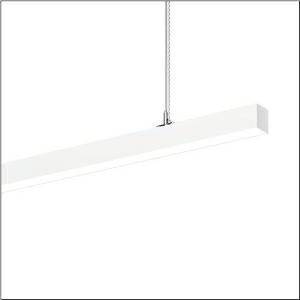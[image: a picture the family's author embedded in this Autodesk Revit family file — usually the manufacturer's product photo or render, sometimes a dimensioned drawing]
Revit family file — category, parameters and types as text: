
# Revit family: silica_r__21_51mx30dc39wb_5262
name_source: partatom
category: Lighting Fixtures
units: mm (PartAtom-declared; Revit-internal decimal feet)

## family parameters
Cut with Voids When Loaded = No
Host = Face
Light Source = No
Part Type = Normal
Room Calculation Point = No
Round Connector Dimension = Use Diameter
Shared = No

## types (1)
- --- (1 x LED, 10520 lm, 68.3 W, 3000K)
    Apparent Load = 68 VA
    CIE Flux Codes = 47 79 96 57 100
    Color Rendering = 80
    Color Temperature = 3000K
    Default Elevation = 1800 mm
    Description = Silica® 21, office luminaire, primary optical cover: cover, of PMMA, opal, light emission: direct/indirect distribution, primary light characteristic: symmetric, installation type: suspended mounting, LED, rated luminous flux: 10.520lm, luminous efficacy: 154lm/W, light colour: 830, colour temperature: 3000K, control gear: DALI 2, with terminal, 3+2-pole, max. 2.5mm², mains connection: 220..240V, AC, 50/60Hz, rated input power: 68.3W, luminaire housing, of aluminium, traffic white (RAL 9016), length: 3.004mm, width: 53mm, height: 53mm, protection rating (complete): IP20, insulation class (complete): insulation class I (protective earthing), certification: CE, permissible operating ambient temperature: 0..+35°C, standard: EN 50419, packaging unit: 1 piece
    Height = 53 mm
    Lamp = 1 x LED
    Lamp Light Flux = 10520 lm
    Lamp Power = 68.3 W
    Lamp count = 1
    Length = 3004 mm
    Luminous efficacy = 154 lm/W
    Manufacturer = Siteco
    ModVariant = No
    Model = 51MX30DC39WB
    Mounting Place = Ceiling
    Mounting Type = Pendant
    Number of Poles = 1
    OnlyDefault = Yes
    Power Factor = 1
    Product Name = Silica® 21
    Product group = office luminaire | ceiling pendant
    ProductGroupID = 904
    Protection Class = Protection class I
    Protection Degree = IP 20
    RLX_Detail_Level = 1
    RLX_Emergency_Light_Flux = 0 lm
    RLX_Emergency_Type = 0
    RLX_Emergency_Type_DB = No
    RlxData = <blob elided: 20909 chars, md5=41c3fc0e>
    Socket = socket
    Standby Power = 0 W
    System Light Flux = 10520 lm
    System Power = 68 W
    Type Comments = factory setting: luminous flux: 100 % | dim-lin: 254 | 233 mA
    Type Image = l_1349023.jpg
    URL = http://relux.com
    VarID = @adj_117390
    Voltage = 0 V
    Weight = 0.00 kg
    Width = 53 mm

## geometry (parser evidence)
native form markers: Blend x4, Sweep x11
no freeform markers — native parametric forms only
